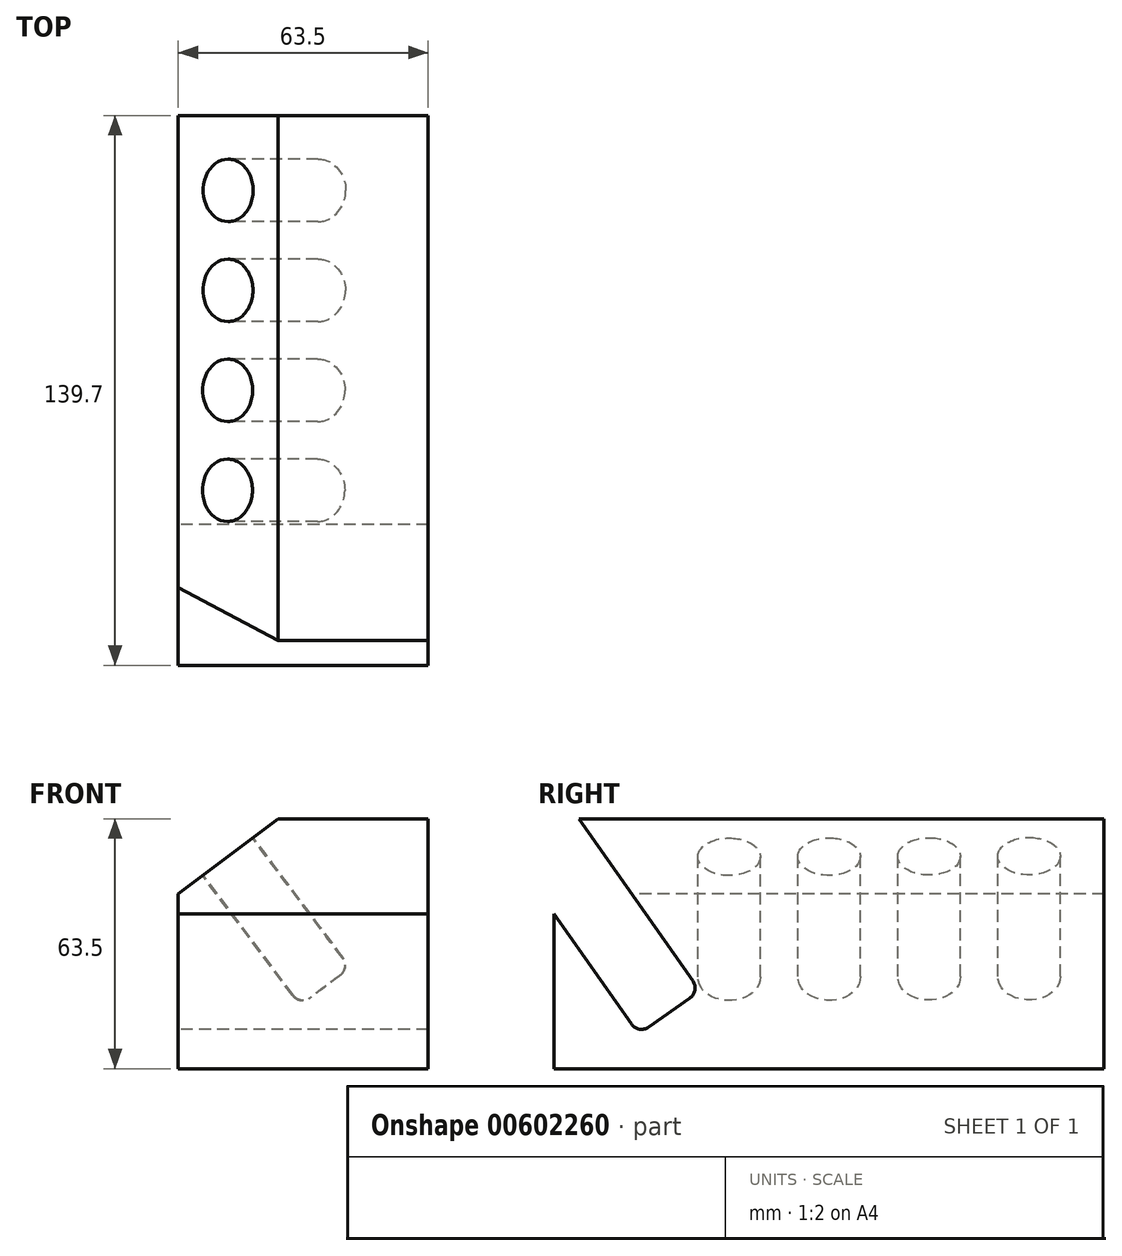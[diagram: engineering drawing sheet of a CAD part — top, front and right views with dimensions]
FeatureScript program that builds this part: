
annotation { "Feature Type Name" : "Feature", "Feature Type Description" : "" }
export const myFeature = defineFeature(function(context is Context, id is Id, definition is map)
    precondition{}
    {
        {
            var Q0;
            Q0=qCreatedBy(makeId("Top.planeOp"),FACE);
            var sketch = newSketch(context, id + "F0", { "sketchPlane" : qUnion([Q0])});
            skLineSegment(sketch, "E0.bottom", {"start": v(31.75, -69.85) * mm, "end": v(-31.75, -69.85) * mm});
            skLineSegment(sketch, "E0.top", {"start": v(31.75, 69.85) * mm, "end": v(-31.75, 69.85) * mm});
            skLineSegment(sketch, "E0.left", {"start": v(31.75, -69.85) * mm, "end": v(31.75, 69.85) * mm});
            skLineSegment(sketch, "E0.right", {"start": v(-31.75, -69.85) * mm, "end": v(-31.75, 69.85) * mm});
            skPoint(sketch, "E0.middle", {"position": v(0, 0) * mm});
            skSolve(sketch);
        }
        {
            var Q0;
            Q0=makeQuery(id+"F0.imprint","IMPRINT",FACE,{"disambiguationData":[TD([[makeQuery(id+"F0.imprint","IMPRINT",EDGE,{"derivedFrom":sQuery(id+"F0.wireOp",EDGE,"E0.bottom")}),-1.0]])]});
            extrude(context, id + "F1", {"entities" : qUnion([Q0]), "depth" : 63.5 * mm, "offsetDistance" : 25.4 * mm});
        }
        {
            var Q0;
            Q0=makeQuery(id+"F1.opExtrude","SWEPT_FACE",FACE,{"disambiguationData":[OSD([sQuery(id+"F0.wireOp",EDGE,"E0.bottom")])]});
            var sketch = newSketch(context, id + "F2", { "sketchPlane" : qUnion([Q0])});
            skLineSegment(sketch, "E1", {"start": v(-31.75, 44.45) * mm, "end": v(-6.35, 63.5) * mm});
            skLineSegment(sketch, "E2", {"start": v(-6.35, 63.5) * mm, "end": v(-31.75, 63.5) * mm});
            skLineSegment(sketch, "E3", {"start": v(-31.75, 63.5) * mm, "end": v(-31.75, 44.45) * mm});
            skSolve(sketch);
        }
        {
            var Q0;
            Q0=makeQuery(id+"F2.imprint","IMPRINT",FACE,{"disambiguationData":[TD([[makeQuery(id+"F2.imprint","IMPRINT",EDGE,{"derivedFrom":sQuery(id+"F2.wireOp",EDGE,"E1")}),1.0]])]});
            extrude(context, id + "F3", {"entities" : qUnion([Q0]), "operationType" : NewBodyOperationType.REMOVE, "endBound" : BoundingType.UP_TO_NEXT, "oppositeDirection" : true, "depth" : 25.4 * mm, "offsetDistance" : 25.4 * mm});
        }
        {
            var Q0;
            Q0=makeQuery(id+"F3.boolean.opBoolean","COPY",FACE,{"derivedFrom":makeQuery(id+"F3.opExtrude","SWEPT_FACE",FACE,{"disambiguationData":[OSD([sQuery(id+"F2.wireOp",EDGE,"E1")])]})});
            var sketch = newSketch(context, id + "F4", { "sketchPlane" : qUnion([Q0])});
            skCircle(sketch, "E4", {"center": v(17.14, 50.8) * mm, "radius": 7.94 * mm});
            skCircle(sketch, "E5.1.0.0", {"center": v(17.06, 25.4) * mm, "radius": 7.94 * mm});
            skCircle(sketch, "E5.2.0.0", {"center": v(16.97, 0) * mm, "radius": 7.94 * mm});
            skCircle(sketch, "E5.3.0.0", {"center": v(16.89, -25.4) * mm, "radius": 7.94 * mm});
            skLineSegment(sketch, "E5.direction1", {"start": v(17.14, 50.8) * mm, "end": v(17.06, 25.4) * mm, "construction": true});
            skSolve(sketch);
        }
        {
            var Q0;
            Q0=makeQuery(id+"F4.imprint","IMPRINT",FACE,{"disambiguationData":[TD([[makeQuery(id+"F4.imprint","IMPRINT",EDGE,{"derivedFrom":sQuery(id+"F4.wireOp",EDGE,"E4")}),1.0]])]});
            var Q1;
            Q1=makeQuery(id+"F4.imprint","IMPRINT",FACE,{"disambiguationData":[TD([[makeQuery(id+"F4.imprint","IMPRINT",EDGE,{"derivedFrom":sQuery(id+"F4.wireOp",EDGE,"E5.1.0.0")}),1.0]])]});
            var Q2;
            Q2=makeQuery(id+"F4.imprint","IMPRINT",FACE,{"disambiguationData":[TD([[makeQuery(id+"F4.imprint","IMPRINT",EDGE,{"derivedFrom":sQuery(id+"F4.wireOp",EDGE,"E5.2.0.0")}),1.0]])]});
            var Q3;
            Q3=makeQuery(id+"F4.imprint","IMPRINT",FACE,{"disambiguationData":[TD([[makeQuery(id+"F4.imprint","IMPRINT",EDGE,{"derivedFrom":sQuery(id+"F4.wireOp",EDGE,"E5.3.0.0")}),1.0]])]});
            extrude(context, id + "F5", {"entities" : qUnion([Q0, Q1, Q2, Q3]), "operationType" : NewBodyOperationType.REMOVE, "oppositeDirection" : true, "depth" : 41.27 * mm, "offsetDistance" : 25.4 * mm});
        }
        {
            var Q0;
            Q0=makeQuery(id+"F5.boolean.opBoolean","COPY",EDGE,{"derivedFrom":makeQuery(id+"F5.opExtrude","CAP_EDGE",EDGE,{"disambiguationData":[OSD([sQuery(id+"F4.wireOp",EDGE,"E5.3.0.0")])],"isStart":false})});
            var Q1;
            Q1=makeQuery(id+"F5.boolean.opBoolean","COPY",EDGE,{"derivedFrom":makeQuery(id+"F5.opExtrude","CAP_EDGE",EDGE,{"disambiguationData":[OSD([sQuery(id+"F4.wireOp",EDGE,"E5.2.0.0")])],"isStart":false})});
            var Q2;
            Q2=makeQuery(id+"F5.boolean.opBoolean","COPY",EDGE,{"derivedFrom":makeQuery(id+"F5.opExtrude","CAP_EDGE",EDGE,{"disambiguationData":[OSD([sQuery(id+"F4.wireOp",EDGE,"E5.1.0.0")])],"isStart":false})});
            var Q3;
            Q3=makeQuery(id+"F5.boolean.opBoolean","COPY",EDGE,{"derivedFrom":makeQuery(id+"F5.opExtrude","CAP_EDGE",EDGE,{"disambiguationData":[OSD([sQuery(id+"F4.wireOp",EDGE,"E4")])],"isStart":false})});
            fillet(context, id + "F6", {"entities" : qUnion([Q0, Q1, Q2, Q3]), "radius" : 3.17 * mm, "tangentPropagation" : true, "allowEdgeOverflow" : false});
        }
        {
            var Q0;
            Q0=makeQuery(id+"F1.opExtrude","SWEPT_FACE",FACE,{"disambiguationData":[OSD([sQuery(id+"F0.wireOp",EDGE,"E0.left")])]});
            var sketch = newSketch(context, id + "F7", { "sketchPlane" : qUnion([Q0])});
            skLineSegment(sketch, "E6", {"start": v(-69.85, 39.36) * mm, "end": v(-48.41, 8.74) * mm});
            skLineSegment(sketch, "E7", {"start": v(-48.41, 8.74) * mm, "end": v(-32.8, 19.67) * mm});
            skLineSegment(sketch, "E8", {"start": v(-32.8, 19.67) * mm, "end": v(-63.5, 63.5) * mm});
            skLineSegment(sketch, "E9", {"start": v(-63.5, 63.5) * mm, "end": v(-69.85, 63.5) * mm});
            skLineSegment(sketch, "E10", {"start": v(-69.85, 63.5) * mm, "end": v(-69.85, 39.36) * mm});
            skSolve(sketch);
        }
        {
            var Q0;
            Q0=makeQuery(id+"F7.imprint","IMPRINT",FACE,{"disambiguationData":[TD([[makeQuery(id+"F7.imprint","IMPRINT",EDGE,{"derivedFrom":sQuery(id+"F7.wireOp",EDGE,"E6")}),1.0]])]});
            extrude(context, id + "F8", {"entities" : qUnion([Q0]), "operationType" : NewBodyOperationType.REMOVE, "endBound" : BoundingType.UP_TO_NEXT, "oppositeDirection" : true, "depth" : 25.4 * mm, "offsetDistance" : 25.4 * mm});
        }
        {
            var Q0;
            Q0=makeQuery(id+"F8.boolean.opBoolean","COPY",EDGE,{"derivedFrom":makeQuery(id+"F8.opExtrude","SWEPT_EDGE",EDGE,{"disambiguationData":[OSD([sQuery(id+"F7.wireOp",EDGE,"E7"),sQuery(id+"F7.wireOp",EDGE,"E8")])]})});
            var Q1;
            Q1=makeQuery(id+"F8.boolean.opBoolean","COPY",EDGE,{"derivedFrom":makeQuery(id+"F8.opExtrude","SWEPT_EDGE",EDGE,{"disambiguationData":[OSD([sQuery(id+"F7.wireOp",EDGE,"E6"),sQuery(id+"F7.wireOp",EDGE,"E7")])]})});
            fillet(context, id + "F9", {"entities" : qUnion([Q0, Q1]), "radius" : 3.17 * mm, "tangentPropagation" : true, "allowEdgeOverflow" : false});
        }
    });
